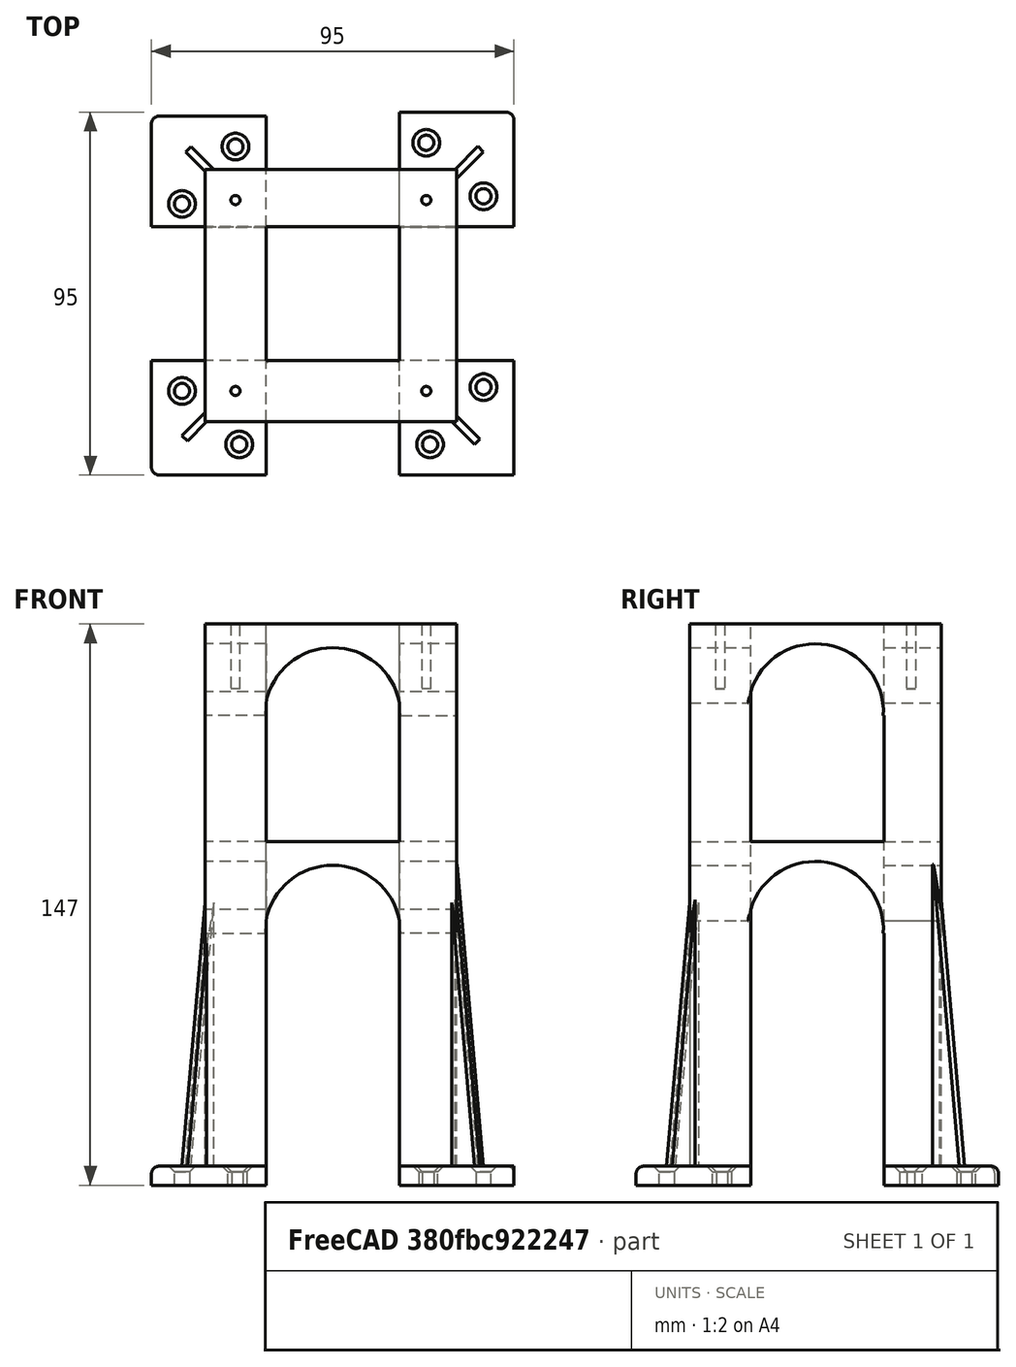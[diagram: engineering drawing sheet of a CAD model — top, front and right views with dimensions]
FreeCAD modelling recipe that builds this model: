
FCSTD DOCUMENT  (FreeCAD 0.20R29603 (Git))
Label: Torre_Lanzadera
License: All rights reserved
LicenseURL: http://en.wikipedia.org/wiki/All_rights_reserved
objects: Part::Cut×36, Part::Box×31, Part::Cylinder×22, Part::MultiFuse×16, Part::Chamfer×10, Part::Fillet×9
note: 124 computed .brp shape members not serialized (recipe doc carries the construction recipe); baked Part::Feature solids carry a one-line shape summary decoded from their .brp

FEATURE [Part::Box] Box054  label="Cubo054"
  AttacherType = Attacher::AttachEngine3D
  Height = 85
  Length = 66
  Placement = pos=(-33,-33,-77) rot=(0,0,1;0rad)
  Width = 66
FEATURE [Part::Box] Box055  label="Cubo055"
  AttacherType = Attacher::AttachEngine3D
  Height = 8
  Length = 50
  Placement = pos=(-25,-25,0) rot=(0,0,1;0rad)
  Width = 50
FEATURE [Part::Box] Box056  label="Cubo056"
  AttacherType = Attacher::AttachEngine3D
  Height = 89
  Length = 35
  Placement = pos=(-17,-17,-81) rot=(0,0,1;0rad)
  Width = 35
FEATURE [Part::Box] Box057  label="Cubo057"
  AttacherType = Attacher::AttachEngine3D
  Height = 89
  Length = 80
  Placement = pos=(-39,-17,-100) rot=(0,0,1;0rad)
  Width = 35
FEATURE [Part::Box] Box058  label="Cubo058"
  AttacherType = Attacher::AttachEngine3D
  Height = 89
  Length = 35
  Placement = pos=(-17,-40,-100) rot=(0,0,1;0rad)
  Width = 100
FEATURE [Part::Box] Box059  label="Cubo059"
  AttacherType = Attacher::AttachEngine3D
  Height = 10
  Length = 51
  Placement = pos=(-25,-25.5,0) rot=(0,0,1;0rad)
  Width = 51
FEATURE [Part::Box] Box060  label="Cubo060"
  AttacherType = Attacher::AttachEngine3D
  Height = 5
  Length = 30
  Placement = pos=(18,-47,-77) rot=(0,0,1;0rad)
  Width = 30
FEATURE [Part::Box] Box061  label="Cubo061"
  AttacherType = Attacher::AttachEngine3D
  Height = 80
  Length = 2
  Placement = pos=(39,-39,-73) rot=(0,0,1;0rad)
  Width = 10
FEATURE [Part::Box] Box062  label="Cubo062"
  AttacherType = Attacher::AttachEngine3D
  Height = 150
  Length = 5
  Placement = pos=(39,-52.5,-100) rot=(-1,0,0;0.122173rad)
  Width = 10
FEATURE [Part::Box] Box063  label="Cubo063"
  AttacherType = Attacher::AttachEngine3D
  Height = 5
  Length = 30
  Placement = pos=(18,-47,-77) rot=(0,0,1;0rad)
  Width = 30
FEATURE [Part::Box] Box064  label="Cubo064"
  AttacherType = Attacher::AttachEngine3D
  Height = 80
  Length = 2
  Placement = pos=(39,-39,-73) rot=(0,0,1;0rad)
  Width = 10
FEATURE [Part::Box] Box065  label="Cubo065"
  AttacherType = Attacher::AttachEngine3D
  Height = 150
  Length = 5
  Placement = pos=(39,-52.5,-100) rot=(-1,0,0;0.122173rad)
  Width = 10
FEATURE [Part::Box] Box066  label="Cubo066"
  AttacherType = Attacher::AttachEngine3D
  Height = 5
  Length = 30
  Placement = pos=(18,-47,-77) rot=(0,0,1;0rad)
  Width = 30
FEATURE [Part::Box] Box067  label="Cubo067"
  AttacherType = Attacher::AttachEngine3D
  Height = 80
  Length = 2
  Placement = pos=(39,-39,-73) rot=(0,0,1;0rad)
  Width = 10
FEATURE [Part::Box] Box068  label="Cubo068"
  AttacherType = Attacher::AttachEngine3D
  Height = 150
  Length = 5
  Placement = pos=(39,-52.5,-100) rot=(-1,0,0;0.122173rad)
  Width = 10
FEATURE [Part::Box] Box069  label="Cubo069"
  AttacherType = Attacher::AttachEngine3D
  Height = 5
  Length = 30
  Placement = pos=(18,-47,-77) rot=(0,0,1;0rad)
  Width = 30
FEATURE [Part::Box] Box070  label="Cubo070"
  AttacherType = Attacher::AttachEngine3D
  Height = 80
  Length = 2
  Placement = pos=(39,-39,-73) rot=(0,0,1;0rad)
  Width = 10
FEATURE [Part::Box] Box071  label="Cubo071"
  AttacherType = Attacher::AttachEngine3D
  Height = 150
  Length = 5
  Placement = pos=(39,-52.5,-100) rot=(-1,0,0;0.122173rad)
  Width = 10
FEATURE [Part::Box] Box072  label="Cubo072"
  AttacherType = Attacher::AttachEngine3D
  Height = 5
  Length = 30
  Placement = pos=(18,-47,-77) rot=(0,0,1;0rad)
  Width = 30
FEATURE [Part::Box] Box073  label="Cubo073"
  AttacherType = Attacher::AttachEngine3D
  Height = 80
  Length = 2
  Placement = pos=(39,-39,-73) rot=(0,0,1;0rad)
  Width = 10
FEATURE [Part::Box] Box074  label="Cubo074"
  AttacherType = Attacher::AttachEngine3D
  Height = 150
  Length = 5
  Placement = pos=(39,-52.5,-100) rot=(-1,0,0;0.122173rad)
  Width = 10
FEATURE [Part::Box] Box075  label="Cubo075"
  AttacherType = Attacher::AttachEngine3D
  Height = 10
  Length = 60
  Placement = pos=(-49,-42,-80) rot=(0,0,1;0rad)
  Width = 60
FEATURE [Part::Box] Box076  label="Cubo076"
  AttacherType = Attacher::AttachEngine3D
  Height = 100
  Length = 35
  Placement = pos=(103,-37,0) rot=(0,0,1;0rad)
  Width = 74
FEATURE [Part::Box] Box077  label="Cubo077"
  AttacherType = Attacher::AttachEngine3D
  Height = 100
  Length = 35
  Placement = pos=(156,-17,0) rot=(0,0,1;1.5708rad)
  Width = 74
FEATURE [Part::Box] Box078  label="Cubo078"
  AttacherType = Attacher::AttachEngine3D
  Height = 78
  Length = 16
  Placement = pos=(87,18,66) rot=(0,0,1;0rad)
  Width = 15
FEATURE [Part::Box] Box081  label="Cubo081"
  AttacherType = Attacher::AttachEngine3D
  Height = 24
  Length = 66
  Placement = pos=(87,-33,123) rot=(0,0,1;0rad)
  Width = 66
FEATURE [Part::Box] Box082  label="Cubo082"
  AttacherType = Attacher::AttachEngine3D
  Height = 78
  Length = 15
  Placement = pos=(138,18,66) rot=(0,0,1;0rad)
  Width = 15
FEATURE [Part::Box] Box083  label="Cubo083"
  AttacherType = Attacher::AttachEngine3D
  Height = 78
  Length = 15
  Placement = pos=(138,-33,66) rot=(0,0,1;0rad)
  Width = 16
FEATURE [Part::Box] Box084  label="Cubo084"
  AttacherType = Attacher::AttachEngine3D
  Height = 78
  Length = 16
  Placement = pos=(87,-33,66) rot=(0,0,1;0rad)
  Width = 16
FEATURE [Part::Box] Box085  label="Cubo085"
  AttacherType = Attacher::AttachEngine3D
  Height = 24
  Length = 66
  Placement = pos=(87,-33,123) rot=(0,0,1;0rad)
  Width = 66
FEATURE [Part::Box] Box086  label="Cubo086"
  AttacherType = Attacher::AttachEngine3D
  Height = 200
  Length = 35
  Placement = pos=(103,-17,0) rot=(0,0,1;0rad)
  Width = 35
FEATURE [Part::Cut] Cut040
  Base = -> Box054
  Tool = -> Box055
FEATURE [Part::Cut] Cut041
  Base = -> Cut040
  Tool = -> Box056
FEATURE [Part::Cut] Cut042
  Base = -> Cut041
  Tool = -> Box057
FEATURE [Part::Cut] Cut043
  Base = -> Cut042
  Tool = -> Box058
FEATURE [Part::Cut] Cut044
  Base = -> Cut043
  Tool = -> Box059
FEATURE [Part::Cut] Cut045
  Base = -> Box061
  Placement = pos=(-17.5,-39,0) rot=(0,0,1;0.785398rad)
  Tool = -> Box062
FEATURE [Part::Cut] Cut048
  Base = -> Box064
  Placement = pos=(-17.5,-39,0) rot=(0,0,1;0.785398rad)
  Tool = -> Box065
FEATURE [Part::Cut] Cut051
  Base = -> Box067
  Placement = pos=(-17.5,-39,0) rot=(0,0,1;0.785398rad)
  Tool = -> Box068
FEATURE [Part::Cut] Cut054
  Base = -> Box070
  Placement = pos=(-17.5,-39,0) rot=(0,0,1;0.785398rad)
  Tool = -> Box071
FEATURE [Part::Cut] Cut057
  Base = -> Box073
  Placement = pos=(-17.5,-39,0) rot=(0,0,1;0.785398rad)
  Tool = -> Box074
FEATURE [Part::Cylinder] Cylinder034  label="Cilindro034"
  Angle = 360
  AttacherType = Attacher::AttachEngine3D
  FirstAngle = 0
  Height = 10
  Placement = pos=(40,-24,-80) rot=(0,0,1;0rad)
  Radius = 2
  SecondAngle = 0
FEATURE [Part::Cylinder] Cylinder035  label="Cilindro035"
  Angle = 360
  AttacherType = Attacher::AttachEngine3D
  FirstAngle = 0
  Height = 10
  Placement = pos=(26,-39,-80) rot=(0,0,1;0rad)
  Radius = 2
  SecondAngle = 0
FEATURE [Part::Cylinder] Cylinder036  label="Cilindro036"
  Angle = 360
  AttacherType = Attacher::AttachEngine3D
  FirstAngle = 0
  Height = 10
  Placement = pos=(40,-24,-80) rot=(0,0,1;0rad)
  Radius = 2
  SecondAngle = 0
FEATURE [Part::Cylinder] Cylinder037  label="Cilindro037"
  Angle = 360
  AttacherType = Attacher::AttachEngine3D
  FirstAngle = 0
  Height = 10
  Placement = pos=(26,-39,-80) rot=(0,0,1;0rad)
  Radius = 2
  SecondAngle = 0
FEATURE [Part::Cylinder] Cylinder038  label="Cilindro038"
  Angle = 360
  AttacherType = Attacher::AttachEngine3D
  FirstAngle = 0
  Height = 10
  Placement = pos=(40,-24,-80) rot=(0,0,1;0rad)
  Radius = 2
  SecondAngle = 0
FEATURE [Part::Cylinder] Cylinder039  label="Cilindro039"
  Angle = 360
  AttacherType = Attacher::AttachEngine3D
  FirstAngle = 0
  Height = 10
  Placement = pos=(26,-39,-80) rot=(0,0,1;0rad)
  Radius = 2
  SecondAngle = 0
FEATURE [Part::Cylinder] Cylinder040  label="Cilindro040"
  Angle = 360
  AttacherType = Attacher::AttachEngine3D
  FirstAngle = 0
  Height = 10
  Placement = pos=(40,-24,-80) rot=(0,0,1;0rad)
  Radius = 2
  SecondAngle = 0
FEATURE [Part::Cylinder] Cylinder041  label="Cilindro041"
  Angle = 360
  AttacherType = Attacher::AttachEngine3D
  FirstAngle = 0
  Height = 10
  Placement = pos=(26,-39,-80) rot=(0,0,1;0rad)
  Radius = 2
  SecondAngle = 0
FEATURE [Part::Cylinder] Cylinder042  label="Cilindro042"
  Angle = 360
  AttacherType = Attacher::AttachEngine3D
  FirstAngle = 0
  Height = 10
  Placement = pos=(40,-24,-80) rot=(0,0,1;0rad)
  Radius = 2
  SecondAngle = 0
FEATURE [Part::Cylinder] Cylinder043  label="Cilindro043"
  Angle = 360
  AttacherType = Attacher::AttachEngine3D
  FirstAngle = 0
  Height = 10
  Placement = pos=(26,-39,-80) rot=(0,0,1;0rad)
  Radius = 2
  SecondAngle = 0
FEATURE [Part::Cylinder] Cylinder044  label="Cilindro044"
  Angle = 360
  AttacherType = Attacher::AttachEngine3D
  FirstAngle = 0
  Height = 10
  Placement = pos=(-19,-19,-9) rot=(0,0,1;0rad)
  Radius = 1.2
  SecondAngle = 0
FEATURE [Part::Cylinder] Cylinder045  label="Cilindro045"
  Angle = 360
  AttacherType = Attacher::AttachEngine3D
  FirstAngle = 0
  Height = 10
  Placement = pos=(19,-19,-9) rot=(0,0,1;0rad)
  Radius = 1.2
  SecondAngle = 0
FEATURE [Part::Cylinder] Cylinder046  label="Cilindro046"
  Angle = 360
  AttacherType = Attacher::AttachEngine3D
  FirstAngle = 0
  Height = 10
  Placement = pos=(19,19,-9) rot=(0,0,1;0rad)
  Radius = 1.2
  SecondAngle = 0
FEATURE [Part::Cylinder] Cylinder047  label="Cilindro047"
  Angle = 360
  AttacherType = Attacher::AttachEngine3D
  FirstAngle = 0
  Height = 10
  Placement = pos=(-19,19,-9) rot=(0,0,1;0rad)
  Radius = 1.2
  SecondAngle = 0
FEATURE [Part::Cylinder] Cylinder049  label="Cilindro049"
  Angle = 360
  AttacherType = Attacher::AttachEngine3D
  FirstAngle = 0
  Height = 80
  Placement = pos=(120.5,39,123) rot=(1,0,0;1.5708rad)
  Radius = 17.8
  SecondAngle = 0
FEATURE [Part::Cut] Cut069
  Base = -> Box081
  Tool = -> Cylinder049
FEATURE [Part::Cylinder] Cylinder050  label="Cilindro050"
  Angle = 360
  AttacherType = Attacher::AttachEngine3D
  FirstAngle = 0
  Height = 83
  Placement = pos=(76.5,0,124) rot=(0,1,0;1.5708rad)
  Radius = 17.8
  SecondAngle = 0
FEATURE [Part::Cut] Cut070
  Base = -> Cut069
  Tool = -> Cylinder050
FEATURE [Part::Cylinder] Cylinder051  label="Cilindro051"
  Angle = 360
  AttacherType = Attacher::AttachEngine3D
  FirstAngle = 0
  Height = 80
  Placement = pos=(120.5,39,123) rot=(1,0,0;1.5708rad)
  Radius = 17.8
  SecondAngle = 0
FEATURE [Part::Cut] Cut071
  Base = -> Box085
  Tool = -> Cylinder051
FEATURE [Part::Cylinder] Cylinder052  label="Cilindro052"
  Angle = 360
  AttacherType = Attacher::AttachEngine3D
  FirstAngle = 0
  Height = 83
  Placement = pos=(76.5,0,124) rot=(0,1,0;1.5708rad)
  Radius = 17.8
  SecondAngle = 0
FEATURE [Part::Cut] Cut072
  Base = -> Cut071
  Placement = pos=(0,0,-57) rot=(0,0,1;0rad)
  Tool = -> Cylinder052
FEATURE [Part::Cylinder] Cylinder057  label="Cilindro057"
  Angle = 360
  AttacherType = Attacher::AttachEngine3D
  FirstAngle = 0
  Height = 40
  Placement = pos=(95,-25,130) rot=(0,0,1;0rad)
  Radius = 1.2
  SecondAngle = 0
FEATURE [Part::Cylinder] Cylinder058  label="Cilindro058"
  Angle = 360
  AttacherType = Attacher::AttachEngine3D
  FirstAngle = 0
  Height = 40
  Placement = pos=(145,25,130) rot=(0,0,1;0rad)
  Radius = 1.2
  SecondAngle = 0
FEATURE [Part::Cylinder] Cylinder059  label="Cilindro059"
  Angle = 360
  AttacherType = Attacher::AttachEngine3D
  FirstAngle = 0
  Height = 40
  Placement = pos=(95,25,130) rot=(0,0,1;0rad)
  Radius = 1.2
  SecondAngle = 0
FEATURE [Part::Cylinder] Cylinder060  label="Cilindro060"
  Angle = 360
  AttacherType = Attacher::AttachEngine3D
  FirstAngle = 0
  Height = 40
  Placement = pos=(145,-25,130) rot=(0,0,1;0rad)
  Radius = 1.2
  SecondAngle = 0
FEATURE [Part::MultiFuse] Fusion045
  Shapes = -> [Box060,Cut045]
FEATURE [Part::Cut] Cut046
  Base = -> Fusion045
  Tool = -> Cylinder034
FEATURE [Part::Cut] Cut047
  Base = -> Cut046
  Tool = -> Cylinder035
FEATURE [Part::Chamfer] Chamfer019
  Base = -> Cut047
  Edges = 1 edges r=1.5: [Edge10]
FEATURE [Part::Chamfer] Chamfer020
  Base = -> Chamfer019
  Edges = 1 edges r=1.5: [Edge10]
FEATURE [Part::Fillet] Fillet018
  Base = -> Chamfer020
  Edges = 1 edges r=2: [Edge4]
FEATURE [Part::Fillet] Fillet183
  Base = -> Fillet018
  Edges = 1 edges r=2: [Edge3]
FEATURE [Part::MultiFuse] Fusion046
  Shapes = -> [Box063,Cut048]
FEATURE [Part::Cut] Cut049
  Base = -> Fusion046
  Tool = -> Cylinder036
FEATURE [Part::Cut] Cut050
  Base = -> Cut049
  Tool = -> Cylinder037
FEATURE [Part::Chamfer] Chamfer021
  Base = -> Cut050
  Edges = 1 edges r=1.5: [Edge10]
FEATURE [Part::Chamfer] Chamfer022
  Base = -> Chamfer021
  Edges = 1 edges r=1.5: [Edge10]
FEATURE [Part::Fillet] Fillet184
  Base = -> Chamfer022
  Edges = 1 edges r=2: [Edge4]
FEATURE [Part::Fillet] Fillet185
  Base = -> Fillet184
  Edges = 1 edges r=2: [Edge3]
  Placement = pos=(1,0,0) rot=(0,0,1;1.5708rad)
FEATURE [Part::MultiFuse] Fusion047
  Shapes = -> [Box066,Cut051]
FEATURE [Part::Cut] Cut052
  Base = -> Fusion047
  Tool = -> Cylinder038
FEATURE [Part::Cut] Cut053
  Base = -> Cut052
  Tool = -> Cylinder039
FEATURE [Part::Chamfer] Chamfer023
  Base = -> Cut053
  Edges = 1 edges r=1.5: [Edge10]
FEATURE [Part::Chamfer] Chamfer024
  Base = -> Chamfer023
  Edges = 1 edges r=1.5: [Edge10]
FEATURE [Part::Fillet] Fillet186
  Base = -> Chamfer024
  Edges = 1 edges r=2: [Edge4]
FEATURE [Part::MultiFuse] Fusion048
  Shapes = -> [Box069,Cut054]
FEATURE [Part::Cut] Cut055
  Base = -> Fusion048
  Tool = -> Cylinder040
FEATURE [Part::Cut] Cut056
  Base = -> Cut055
  Tool = -> Cylinder041
FEATURE [Part::Chamfer] Chamfer025
  Base = -> Cut056
  Edges = 1 edges r=1.5: [Edge10]
FEATURE [Part::Chamfer] Chamfer026
  Base = -> Chamfer025
  Edges = 1 edges r=1.5: [Edge10]
FEATURE [Part::Fillet] Fillet023
  Base = -> Chamfer026
  Edges = 1 edges r=2: [Edge4]
FEATURE [Part::Fillet] Fillet024
  Base = -> Fillet023
  Edges = 1 edges r=2: [Edge3]
  Placement = pos=(1,0,0) rot=(0,0,1;3.14159rad)
FEATURE [Part::Cut] Cut060
  Base = -> Fillet024
  Tool = -> Box075
FEATURE [Part::MultiFuse] Fusion049
  Shapes = -> [Box072,Cut057]
FEATURE [Part::Cut] Cut058
  Base = -> Fusion049
  Tool = -> Cylinder042
FEATURE [Part::Cut] Cut059
  Base = -> Cut058
  Tool = -> Cylinder043
FEATURE [Part::Chamfer] Chamfer027
  Base = -> Cut059
  Edges = 1 edges r=1.5: [Edge10]
FEATURE [Part::Chamfer] Chamfer028
  Base = -> Chamfer027
  Edges = 1 edges r=1.5: [Edge10]
FEATURE [Part::Fillet] Fillet025
  Base = -> Chamfer028
  Edges = 1 edges r=2: [Edge4]
FEATURE [Part::Fillet] Fillet026
  Base = -> Fillet025
  Edges = 1 edges r=2: [Edge3]
  Placement = pos=(0,1,0) rot=(0,0,-1;1.5708rad)
FEATURE [Part::MultiFuse] Fusion050
  Shapes = -> [Cut044,Fillet183]
FEATURE [Part::MultiFuse] Fusion051
  Shapes = -> [Fusion050,Cut060]
FEATURE [Part::MultiFuse] Fusion052
  Shapes = -> [Fusion051,Fillet026]
FEATURE [Part::MultiFuse] Fusion053
  Shapes = -> [Fusion052,Fillet186]
FEATURE [Part::MultiFuse] Fusion054  label="BasePricipal001"
  Shapes = -> [Fusion053,Fillet185]
FEATURE [Part::Cut] Cut061
  Base = -> Fusion054
  Tool = -> Cylinder044
FEATURE [Part::Cut] Cut062
  Base = -> Cut061
  Tool = -> Cylinder047
FEATURE [Part::Cut] Cut063
  Base = -> Cut062
  Tool = -> Cylinder046
FEATURE [Part::Cut] Cut064  label="BasePrincipal001"
  Base = -> Cut063
  Placement = pos=(120,0,77) rot=(0,0,1;0rad)
  Tool = -> Cylinder045
FEATURE [Part::Cut] Cut065
  Base = -> Cut064
  Tool = -> Box076
FEATURE [Part::Cut] Cut066
  Base = -> Cut065
  Tool = -> Box077
FEATURE [Part::MultiFuse] Fusion055
  Shapes = -> [Cut066,Box082]
FEATURE [Part::MultiFuse] Fusion056
  Shapes = -> [Fusion055,Box084]
FEATURE [Part::MultiFuse] Fusion057
  Shapes = -> [Fusion056,Box083]
FEATURE [Part::MultiFuse] Fusion058
  Shapes = -> [Fusion057,Box078]
FEATURE [Part::MultiFuse] Fusion059
  Shapes = -> [Fusion058,Cut070]
FEATURE [Part::MultiFuse] Fusion060
  Shapes = -> [Cut072,Fusion059]
FEATURE [Part::Cut] Cut073  label="Torre"
  Base = -> Fusion060
  Tool = -> Box086
FEATURE [Part::Cut] Cut081
  Base = -> Cut073
  Tool = -> Cylinder057
FEATURE [Part::Cut] Cut082
  Base = -> Cut081
  Tool = -> Cylinder060
FEATURE [Part::Cut] Cut083
  Base = -> Cut082
  Tool = -> Cylinder059
FEATURE [Part::Cut] Cut084  label="Torre_Lanzadera"
  Base = -> Cut083
  Placement = pos=(-120,0,-55) rot=(0,0,1;0rad)
  Tool = -> Cylinder058
